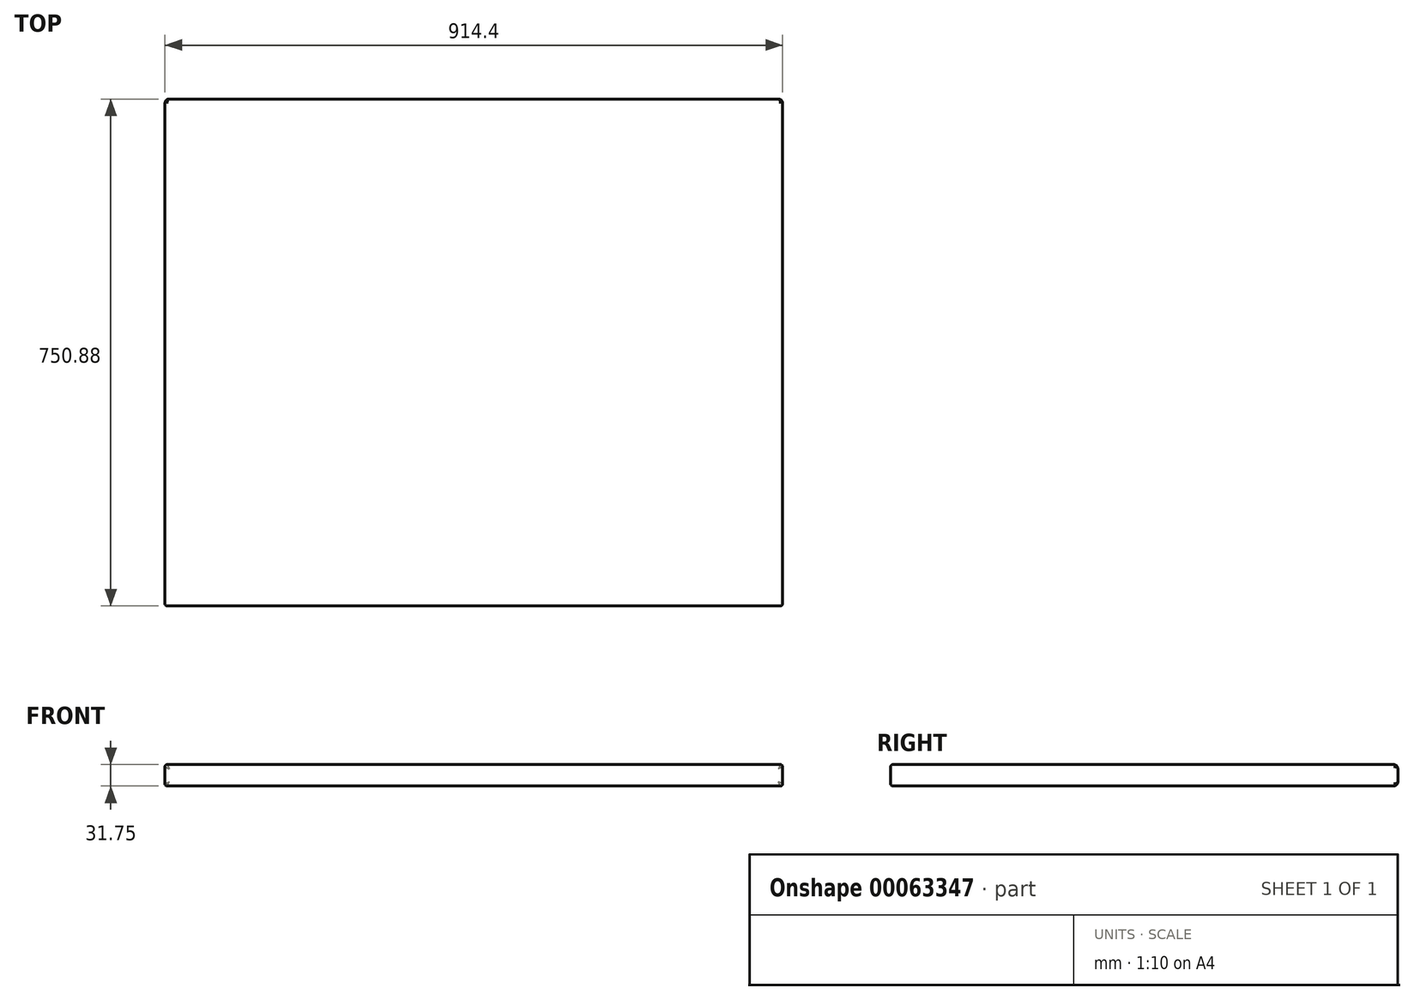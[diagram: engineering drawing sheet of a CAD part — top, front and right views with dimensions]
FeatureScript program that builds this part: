
annotation { "Feature Type Name" : "Feature", "Feature Type Description" : "" }
export const myFeature = defineFeature(function(context is Context, id is Id, definition is map)
    precondition{}
    {
        {
            var Q0;
            Q0=qCreatedBy(makeId("Top.planeOp"),FACE);
            var sketch = newSketch(context, id + "F0", { "sketchPlane" : qUnion([Q0])});
            skLineSegment(sketch, "E0.rect.bottom", {"start": v(457.2, -375.44) * mm, "end": v(-457.2, -375.44) * mm});
            skLineSegment(sketch, "E0.rect.top", {"start": v(457.2, 375.44) * mm, "end": v(-457.2, 375.44) * mm});
            skLineSegment(sketch, "E0.rect.left", {"start": v(457.2, -375.44) * mm, "end": v(457.2, 375.44) * mm});
            skLineSegment(sketch, "E0.rect.right", {"start": v(-457.2, -375.44) * mm, "end": v(-457.2, 375.44) * mm});
            skPoint(sketch, "E0.rect.middle", {"position": v(0, 0) * mm});
            skSolve(sketch);
        }
        {
            var Q0;
            Q0 = qSketchRegion(id + "F0", true);
            extrude(context, id + "F1", {"entities" : qUnion([Q0]), "depth" : 31.75 * mm});
        }
        {
            var Q0;
            Q0=makeQuery(id+"F1.opExtrude","CAP_EDGE",EDGE,{"disambiguationData":[OSD([sQuery(id+"F0.wireOp",EDGE,"E0.rect.right")])],"isStart":false});
            var Q1;
            Q1=makeQuery(id+"F1.opExtrude","CAP_EDGE",EDGE,{"disambiguationData":[OSD([sQuery(id+"F0.wireOp",EDGE,"E0.rect.bottom")])],"isStart":false});
            var Q2;
            Q2=makeQuery(id+"F1.opExtrude","CAP_EDGE",EDGE,{"disambiguationData":[OSD([sQuery(id+"F0.wireOp",EDGE,"E0.rect.left")])],"isStart":false});
            var Q3;
            Q3=makeQuery(id+"F1.opExtrude","CAP_EDGE",EDGE,{"disambiguationData":[OSD([sQuery(id+"F0.wireOp",EDGE,"E0.rect.left")])],"isStart":true});
            var Q4;
            Q4=makeQuery(id+"F1.opExtrude","CAP_EDGE",EDGE,{"disambiguationData":[OSD([sQuery(id+"F0.wireOp",EDGE,"E0.rect.bottom")])],"isStart":true});
            var Q5;
            Q5=makeQuery(id+"F1.opExtrude","CAP_EDGE",EDGE,{"disambiguationData":[OSD([sQuery(id+"F0.wireOp",EDGE,"E0.rect.right")])],"isStart":true});
            var Q6;
            Q6=makeQuery(id+"F1.opExtrude","SWEPT_EDGE",EDGE,{"disambiguationData":[OSD([sQuery(id+"F0.wireOp",EDGE,"E0.rect.bottom"),sQuery(id+"F0.wireOp",EDGE,"E0.rect.right")])]});
            var Q7;
            Q7=makeQuery(id+"F1.opExtrude","SWEPT_EDGE",EDGE,{"disambiguationData":[OSD([sQuery(id+"F0.wireOp",EDGE,"E0.rect.bottom"),sQuery(id+"F0.wireOp",EDGE,"E0.rect.left")])]});
            fillet(context, id + "F2", {"entities" : qUnion([Q0, Q1, Q2, Q3, Q4, Q5, Q6, Q7]), "radius" : 3.17 * mm, "tangentPropagation" : true, "allowEdgeOverflow" : false});
        }
        {
            var Q0;
            Q0=makeQuery(id+"F1.opExtrude","CAP_EDGE",EDGE,{"disambiguationData":[OSD([sQuery(id+"F0.wireOp",EDGE,"E0.rect.top")])],"isStart":false});
            var Q1;
            Q1=makeQuery(id+"F1.opExtrude","CAP_EDGE",EDGE,{"disambiguationData":[OSD([sQuery(id+"F0.wireOp",EDGE,"E0.rect.top")])],"isStart":true});
            var Q2;
            Q2=makeQuery(id+"F1.opExtrude","SWEPT_EDGE",EDGE,{"disambiguationData":[OSD([sQuery(id+"F0.wireOp",EDGE,"E0.rect.top"),sQuery(id+"F0.wireOp",EDGE,"E0.rect.right")])]});
            var Q3;
            Q3=makeQuery(id+"F1.opExtrude","SWEPT_EDGE",EDGE,{"disambiguationData":[OSD([sQuery(id+"F0.wireOp",EDGE,"E0.rect.top"),sQuery(id+"F0.wireOp",EDGE,"E0.rect.left")])]});
            var Q4;
            Q4=makeQuery(id+"F2.opFillet","BLEND_EDGE",EDGE,{"blendedFrom":[makeQuery(id+"F1.opExtrude","CAP_EDGE",EDGE,{"disambiguationData":[OSD([sQuery(id+"F0.wireOp",EDGE,"E0.rect.left")])],"isStart":false}),makeQuery(id+"F1.opExtrude","SWEPT_FACE",FACE,{"disambiguationData":[OSD([sQuery(id+"F0.wireOp",EDGE,"E0.rect.top")])]})],"blendedInto":[makeQuery(id+"F1.opExtrude","SWEPT_FACE",FACE,{"disambiguationData":[OSD([sQuery(id+"F0.wireOp",EDGE,"E0.rect.top")])]})]});
            var Q5;
            Q5=makeQuery(id+"F2.opFillet","BLEND_EDGE",EDGE,{"blendedFrom":[makeQuery(id+"F1.opExtrude","CAP_EDGE",EDGE,{"disambiguationData":[OSD([sQuery(id+"F0.wireOp",EDGE,"E0.rect.left")])],"isStart":true}),makeQuery(id+"F1.opExtrude","SWEPT_FACE",FACE,{"disambiguationData":[OSD([sQuery(id+"F0.wireOp",EDGE,"E0.rect.top")])]})],"blendedInto":[makeQuery(id+"F1.opExtrude","SWEPT_FACE",FACE,{"disambiguationData":[OSD([sQuery(id+"F0.wireOp",EDGE,"E0.rect.top")])]})]});
            var Q6;
            Q6=makeQuery(id+"F2.opFillet","BLEND_EDGE",EDGE,{"blendedFrom":[makeQuery(id+"F1.opExtrude","CAP_EDGE",EDGE,{"disambiguationData":[OSD([sQuery(id+"F0.wireOp",EDGE,"E0.rect.right")])],"isStart":true}),makeQuery(id+"F1.opExtrude","SWEPT_FACE",FACE,{"disambiguationData":[OSD([sQuery(id+"F0.wireOp",EDGE,"E0.rect.top")])]})],"blendedInto":[makeQuery(id+"F1.opExtrude","SWEPT_FACE",FACE,{"disambiguationData":[OSD([sQuery(id+"F0.wireOp",EDGE,"E0.rect.top")])]})]});
            var Q7;
            Q7=makeQuery(id+"F2.opFillet","BLEND_EDGE",EDGE,{"blendedFrom":[makeQuery(id+"F1.opExtrude","CAP_EDGE",EDGE,{"disambiguationData":[OSD([sQuery(id+"F0.wireOp",EDGE,"E0.rect.right")])],"isStart":false}),makeQuery(id+"F1.opExtrude","SWEPT_FACE",FACE,{"disambiguationData":[OSD([sQuery(id+"F0.wireOp",EDGE,"E0.rect.top")])]})],"blendedInto":[makeQuery(id+"F1.opExtrude","SWEPT_FACE",FACE,{"disambiguationData":[OSD([sQuery(id+"F0.wireOp",EDGE,"E0.rect.top")])]})]});
            fillet(context, id + "F3", {"entities" : qUnion([Q0, Q1, Q2, Q3, Q4, Q5, Q6, Q7]), "radius" : 6.35 * mm, "tangentPropagation" : true, "allowEdgeOverflow" : false});
        }
    });
